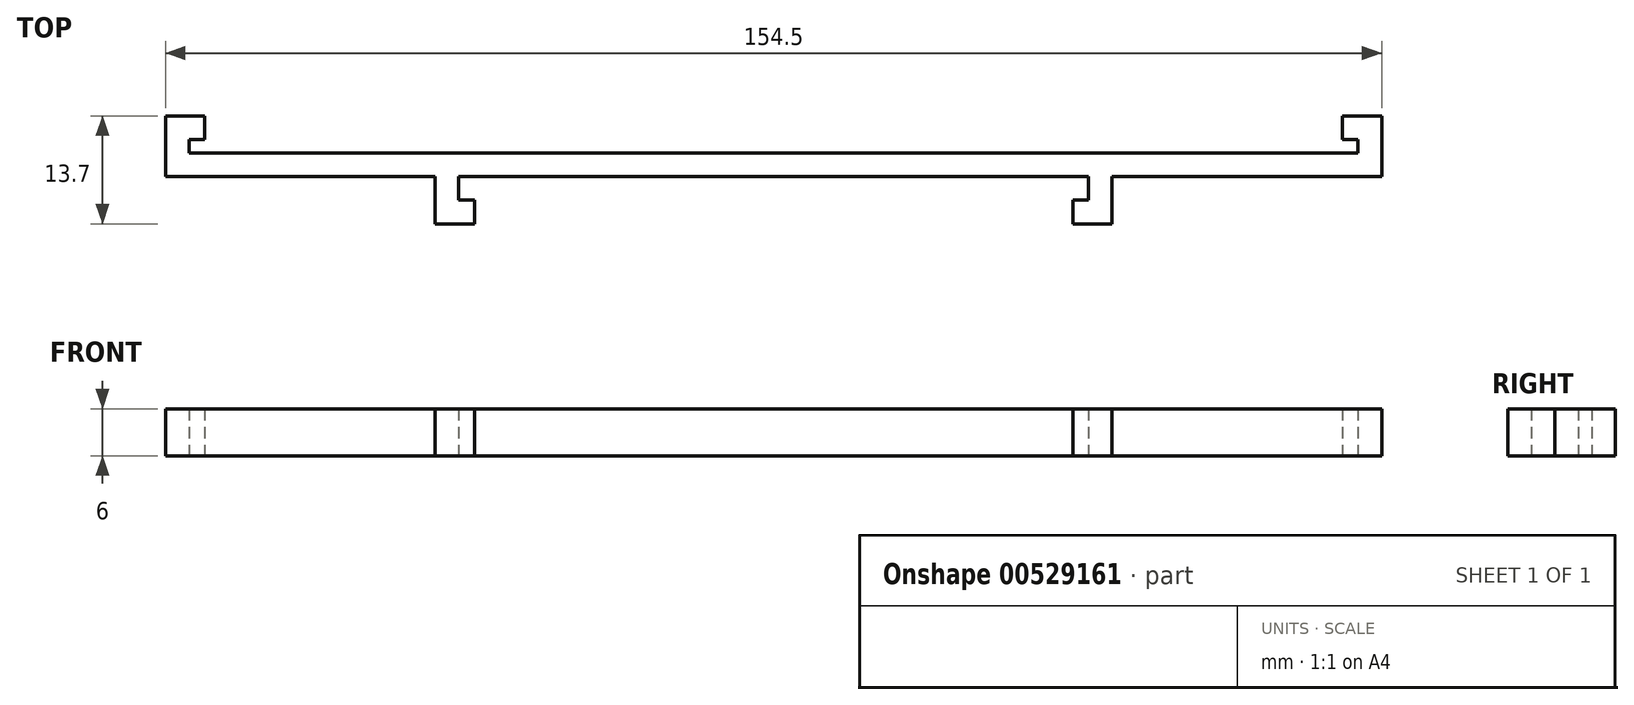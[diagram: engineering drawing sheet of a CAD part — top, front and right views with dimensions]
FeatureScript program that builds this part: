
annotation { "Feature Type Name" : "Feature", "Feature Type Description" : "" }
export const myFeature = defineFeature(function(context is Context, id is Id, definition is map)
    precondition{}
    {
        {
            var Q0;
            Q0=qCreatedBy(makeId("Top.planeOp"),FACE);
            var sketch = newSketch(context, id + "F0", { "sketchPlane" : qUnion([Q0])});
            skLineSegment(sketch, "E0", {"start": v(-88.85, 9.42) * mm, "end": v(81.15, 9.42) * mm, "construction": true});
            skLineSegment(sketch, "E1", {"start": v(-88.85, -7.28) * mm, "end": v(81.15, -7.28) * mm, "construction": true});
            skLineSegment(sketch, "E2", {"start": v(-88.85, 1.72) * mm, "end": v(81.15, 1.72) * mm, "construction": true});
            skLineSegment(sketch, "E3", {"start": v(-77.3, 17.34) * mm, "end": v(-77.3, -16) * mm, "construction": true});
            skLineSegment(sketch, "E4", {"start": v(77.2, 16.82) * mm, "end": v(77.2, -14.78) * mm, "construction": true});
            skLineSegment(sketch, "E5", {"start": v(-74.3, 17.22) * mm, "end": v(-74.3, -16) * mm, "construction": true});
            skLineSegment(sketch, "E6", {"start": v(74.2, 16.82) * mm, "end": v(74.2, -14.78) * mm, "construction": true});
            skLineSegment(sketch, "E7", {"start": v(-88.85, 6.42) * mm, "end": v(81.15, 6.42) * mm, "construction": true});
            skLineSegment(sketch, "E8", {"start": v(-88.85, 4.72) * mm, "end": v(81.15, 4.72) * mm, "construction": true});
            skLineSegment(sketch, "E9", {"start": v(-72.3, 17.22) * mm, "end": v(-72.3, -16) * mm, "construction": true});
            skLineSegment(sketch, "E10", {"start": v(72.2, 16.82) * mm, "end": v(72.2, -14.78) * mm, "construction": true});
            skLineSegment(sketch, "E11", {"start": v(-72.3, 9.42) * mm, "end": v(-77.3, 9.42) * mm});
            skLineSegment(sketch, "E12", {"start": v(-77.3, 9.42) * mm, "end": v(-77.3, 1.72) * mm});
            skLineSegment(sketch, "E13", {"start": v(-77.3, 1.72) * mm, "end": v(-43.05, 1.72) * mm});
            skLineSegment(sketch, "E14", {"start": v(77.2, 1.72) * mm, "end": v(77.2, 9.42) * mm});
            skLineSegment(sketch, "E15", {"start": v(77.2, 9.42) * mm, "end": v(72.2, 9.42) * mm});
            skLineSegment(sketch, "E16", {"start": v(72.2, 9.42) * mm, "end": v(72.2, 6.42) * mm});
            skLineSegment(sketch, "E17", {"start": v(72.2, 6.42) * mm, "end": v(74.2, 6.42) * mm});
            skLineSegment(sketch, "E18", {"start": v(74.2, 6.42) * mm, "end": v(74.2, 4.72) * mm});
            skLineSegment(sketch, "E19", {"start": v(74.2, 4.72) * mm, "end": v(-74.3, 4.72) * mm});
            skLineSegment(sketch, "E20", {"start": v(-74.3, 4.72) * mm, "end": v(-74.3, 6.42) * mm});
            skLineSegment(sketch, "E21", {"start": v(-74.3, 6.42) * mm, "end": v(-72.3, 6.42) * mm});
            skLineSegment(sketch, "E22", {"start": v(-72.3, 6.42) * mm, "end": v(-72.3, 9.42) * mm});
            skLineSegment(sketch, "E23", {"start": v(-0.05, 22.09) * mm, "end": v(-0.05, -13.48) * mm, "construction": true});
            skLineSegment(sketch, "E24", {"start": v(-40.05, 22.49) * mm, "end": v(-40.05, -15.75) * mm, "construction": true});
            skLineSegment(sketch, "E25.MirrorCS", {"start": v(39.95, 22.49) * mm, "end": v(39.95, -15.75) * mm, "construction": true});
            skLineSegment(sketch, "E26", {"start": v(-49.35, -4.28) * mm, "end": v(48.49, -4.28) * mm, "construction": true});
            skLineSegment(sketch, "E27", {"start": v(-43.05, 13.03) * mm, "end": v(-43.05, -15.94) * mm, "construction": true});
            skLineSegment(sketch, "E28.MirrorCS", {"start": v(42.95, 13.03) * mm, "end": v(42.95, -15.94) * mm, "construction": true});
            skLineSegment(sketch, "E29", {"start": v(-55.61, -1.28) * mm, "end": v(50.64, -1.28) * mm, "construction": true});
            skLineSegment(sketch, "E30", {"start": v(-38.05, 13.03) * mm, "end": v(-38.05, -15.94) * mm, "construction": true});
            skLineSegment(sketch, "E31.MirrorCS", {"start": v(37.95, 13.03) * mm, "end": v(37.95, -15.94) * mm, "construction": true});
            skLineSegment(sketch, "E32", {"start": v(-43.05, 1.72) * mm, "end": v(-43.05, -4.28) * mm});
            skLineSegment(sketch, "E33", {"start": v(-43.05, -4.28) * mm, "end": v(-38.05, -4.28) * mm});
            skLineSegment(sketch, "E34", {"start": v(-38.05, -4.28) * mm, "end": v(-38.05, -1.28) * mm});
            skLineSegment(sketch, "E35", {"start": v(-38.05, -1.28) * mm, "end": v(-40.05, -1.28) * mm});
            skLineSegment(sketch, "E36", {"start": v(-40.05, -1.28) * mm, "end": v(-40.05, 1.72) * mm});
            skLineSegment(sketch, "E37", {"start": v(42.95, 1.72) * mm, "end": v(42.95, -4.28) * mm});
            skLineSegment(sketch, "E38", {"start": v(42.95, -4.28) * mm, "end": v(37.95, -4.28) * mm});
            skLineSegment(sketch, "E39", {"start": v(37.95, -4.28) * mm, "end": v(37.95, -1.28) * mm});
            skLineSegment(sketch, "E40", {"start": v(37.95, -1.28) * mm, "end": v(39.95, -1.28) * mm});
            skLineSegment(sketch, "E41", {"start": v(39.95, -1.28) * mm, "end": v(39.95, 1.72) * mm});
            skLineSegment(sketch, "E42.trimOffspring", {"start": v(-40.05, 1.72) * mm, "end": v(39.95, 1.72) * mm});
            skLineSegment(sketch, "E43.trimOffspring", {"start": v(42.95, 1.72) * mm, "end": v(77.2, 1.72) * mm});
            skSolve(sketch);
        }
        {
            var Q0;
            Q0 = qSketchRegion(id + "F0", true);
            extrude(context, id + "F1", {"entities" : qUnion([Q0]), "depth" : 6 * mm, "offsetDistance" : 25 * mm});
        }
    });
